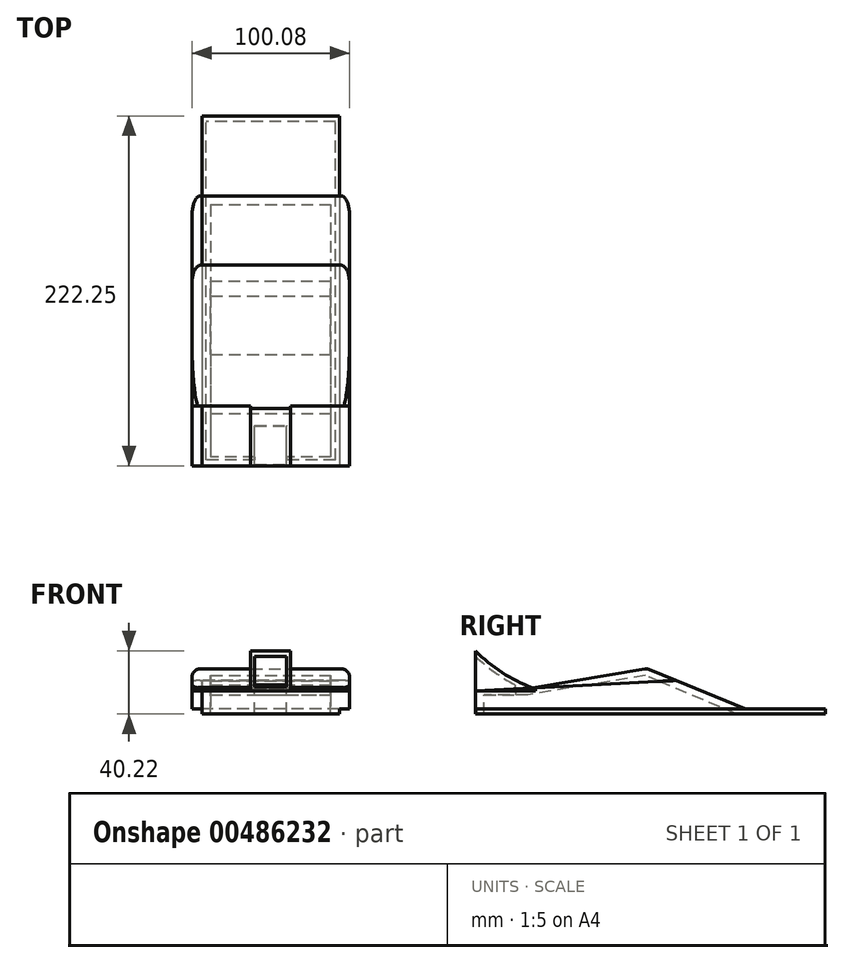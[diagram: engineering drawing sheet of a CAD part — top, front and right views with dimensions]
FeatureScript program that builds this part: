
annotation { "Feature Type Name" : "Feature", "Feature Type Description" : "" }
export const myFeature = defineFeature(function(context is Context, id is Id, definition is map)
    precondition{}
    {
        {
            var Q0;
            Q0=qCreatedBy(makeId("Top.planeOp"),FACE);
            var sketch = newSketch(context, id + "F0", { "sketchPlane" : qUnion([Q0])});
            skLineSegment(sketch, "E0.bottom", {"start": v(43.69, 111.12) * mm, "end": v(-43.69, 111.12) * mm});
            skLineSegment(sketch, "E0.top", {"start": v(43.69, -111.13) * mm, "end": v(-43.69, -111.13) * mm});
            skLineSegment(sketch, "E0.left", {"start": v(43.69, 111.12) * mm, "end": v(43.69, -111.13) * mm});
            skLineSegment(sketch, "E0.right", {"start": v(-43.69, 111.12) * mm, "end": v(-43.69, -111.13) * mm});
            skPoint(sketch, "E0.middle", {"position": v(0, 0) * mm});
            skSolve(sketch);
        }
        {
            var Q0;
            Q0 = qSketchRegion(id + "F0", true);
            extrude(context, id + "F1", {"entities" : qUnion([Q0]), "depth" : 3.17 * mm, "offsetDistance" : 25.4 * mm});
        }
        {
            var Q0;
            Q0=makeQuery(id+"F1.opExtrude","SWEPT_FACE",FACE,{"disambiguationData":[OSD([sQuery(id+"F0.wireOp",EDGE,"E0.right")])]});
            var sketch = newSketch(context, id + "F2", { "sketchPlane" : qUnion([Q0])});
            skLineSegment(sketch, "E1", {"start": v(-111.12, 3.18) * mm, "end": v(-60.32, 3.18) * mm, "construction": true});
            skLineSegment(sketch, "E2", {"start": v(-60.32, 3.18) * mm, "end": v(-16.2, 21.3) * mm});
            skLineSegment(sketch, "E3", {"start": v(-16.2, 21.3) * mm, "end": v(111.12, 14.82) * mm});
            skLineSegment(sketch, "E4", {"start": v(111.13, 3.18) * mm, "end": v(111.13, 14.82) * mm});
            skSolve(sketch);
        }
        {
            var Q0;
            {var subQ0=sQuery(id+"F2.wireOp",EDGE,"E2");Q0=makeQuery(id+"F2.imprint","IMPRINT",FACE,{"disambiguationData":[TD([[makeQuery(id+"F2.imprint","IMPRINT",EDGE,{"derivedFrom":subQ0}),-1.0]])]});}
            extrude(context, id + "F3", {"entities" : qUnion([Q0]), "depth" : 6.35 * mm, "offsetDistance" : 25.4 * mm});
        }
        {
            var Q0;
            Q0=makeQuery(id+"F3.opExtrude","CAP_FACE",FACE,{"disambiguationData":[OSD([sQuery(id+"F0.wireOp",EDGE,"E0.right"),sQuery(id+"F2.wireOp",EDGE,"E2"),sQuery(id+"F2.wireOp",EDGE,"E3"),sQuery(id+"F2.wireOp",EDGE,"E4")])],"isStart":true});
            extrude(context, id + "F4", {"entities" : qUnion([Q0]), "depth" : 87.38 * mm, "offsetDistance" : 25.4 * mm});
        }
        {
            var Q0;
            Q0=makeQuery(id+"F4.opExtrude","CAP_FACE",FACE,{"disambiguationData":[OSD([sQuery(id+"F0.wireOp",EDGE,"E0.right"),sQuery(id+"F2.wireOp",EDGE,"E2"),sQuery(id+"F2.wireOp",EDGE,"E3"),sQuery(id+"F2.wireOp",EDGE,"E4")])],"isStart":false});
            extrude(context, id + "F5", {"entities" : qUnion([Q0]), "operationType" : NewBodyOperationType.ADD, "depth" : 6.35 * mm, "offsetDistance" : 25.4 * mm});
        }
        {
            var Q0;
            Q0=makeQuery(id+"F5.opExtrude","CAP_FACE",FACE,{"disambiguationData":[OSD([sQuery(id+"F0.wireOp",EDGE,"E0.right"),sQuery(id+"F2.wireOp",EDGE,"E2"),sQuery(id+"F2.wireOp",EDGE,"E3"),sQuery(id+"F2.wireOp",EDGE,"E4")])],"isStart":false});
            var sketch = newSketch(context, id + "F6", { "sketchPlane" : qUnion([Q0])});
            skLineSegment(sketch, "E5", {"start": v(-111.13, 14.82) * mm, "end": v(-111.13, 40.22) * mm});
            skArc(sketch, "E6", {"start": v(-111.13, 40.22) * mm, "mid": v(-94.32, 26.4) * mm, "end": v(-74.87, 16.67) * mm});
            skLineSegment(sketch, "E7", {"start": v(16.2, 21.3) * mm, "end": v(-2.18, 28.86) * mm});
            skLineSegment(sketch, "E8", {"start": v(-2.18, 28.86) * mm, "end": v(-74.87, 16.67) * mm});
            skSolve(sketch);
        }
        {
            var Q0;
            {var subQ0=sQuery(id+"F6.wireOp",EDGE,"E5");Q0=makeQuery(id+"F6.imprint","IMPRINT",FACE,{"disambiguationData":[TD([[makeQuery(id+"F6.imprint","IMPRINT",EDGE,{"derivedFrom":subQ0}),-1.0]])]});}
            var Q1;
            {var subQ0=sQuery(id+"F6.wireOp",EDGE,"E7");Q1=makeQuery(id+"F6.imprint","IMPRINT",FACE,{"disambiguationData":[TD([[makeQuery(id+"F6.imprint","IMPRINT",EDGE,{"derivedFrom":subQ0}),1.0]])]});}
            extrude(context, id + "F7", {"entities" : qUnion([Q0, Q1]), "oppositeDirection" : true, "depth" : 100.08 * mm, "offsetDistance" : 25.4 * mm});
        }
        {
            var Q0;
            Q0=makeQuery(id+"F7.opExtrude","SWEPT_FACE",FACE,{"disambiguationData":[OSD([sQuery(id+"F6.wireOp",EDGE,"E5")])]});
            var sketch = newSketch(context, id + "F8", { "sketchPlane" : qUnion([Q0])});
            skLineSegment(sketch, "E9", {"start": v(-50.04, 40.22) * mm, "end": v(-50.04, 14.82) * mm});
            skLineSegment(sketch, "E10", {"start": v(-50.04, 45.23) * mm, "end": v(-81.4, 16.65) * mm});
            skLineSegment(sketch, "E11", {"start": v(-81.4, 16.65) * mm, "end": v(-50.04, 14.82) * mm});
            skLineSegment(sketch, "E12.MirrorCS", {"start": v(46.51, 14.82) * mm, "end": v(-4.16, 14.82) * mm});
            skLineSegment(sketch, "E13", {"start": v(0, 14.82) * mm, "end": v(12.7, 14.82) * mm});
            skLineSegment(sketch, "E14", {"start": v(0, 14.82) * mm, "end": v(-12.7, 14.82) * mm});
            skLineSegment(sketch, "E15", {"start": v(-12.7, 14.82) * mm, "end": v(-12.7, 47.79) * mm});
            skLineSegment(sketch, "E16", {"start": v(-12.7, 47.79) * mm, "end": v(-50.04, 45.23) * mm});
            skLineSegment(sketch, "E17", {"start": v(-12.7, 47.79) * mm, "end": v(0, 47.79) * mm});
            skLineSegment(sketch, "E18", {"start": v(0, 47.79) * mm, "end": v(0, 14.82) * mm});
            skLineSegment(sketch, "E19", {"start": v(12.7, 14.82) * mm, "end": v(12.7, 47.79) * mm});
            skLineSegment(sketch, "E20", {"start": v(12.7, 47.79) * mm, "end": v(0, 47.79) * mm});
            skLineSegment(sketch, "E21", {"start": v(12.7, 47.79) * mm, "end": v(40.72, 45.23) * mm});
            skLineSegment(sketch, "E22", {"start": v(46.51, 14.82) * mm, "end": v(-50.04, 14.82) * mm});
            skLineSegment(sketch, "E23", {"start": v(40.72, 45.23) * mm, "end": v(65.13, 48.77) * mm});
            skLineSegment(sketch, "E24", {"start": v(65.13, 48.77) * mm, "end": v(72.08, 16.65) * mm});
            skLineSegment(sketch, "E25", {"start": v(46.51, 14.82) * mm, "end": v(75.86, 14.82) * mm});
            skLineSegment(sketch, "E26", {"start": v(75.86, 14.82) * mm, "end": v(72.08, 16.65) * mm});
            skSolve(sketch);
        }
        {
            var Q0;
            {var subQ4=sQuery(id+"F8.wireOp",EDGE,"E9");Q0=makeQuery(id+"F8.imprint","IMPRINT",FACE,{"disambiguationData":[TD([[makeQuery(id+"F8.imprint","IMPRINT",EDGE,{"derivedFrom":subQ4}),1.0]])]});}
            var Q1;
            {var subQ0=sQuery(id+"F8.wireOp",EDGE,"E9");Q1=makeQuery(id+"F8.imprint","IMPRINT",FACE,{"disambiguationData":[TD([[makeQuery(id+"F8.imprint","IMPRINT",EDGE,{"derivedFrom":subQ0}),-1.0]])]});}
            var Q2;
            {var subQ0=sQuery(id+"F8.wireOp",EDGE,"E12.MirrorCS");var subQ1=sQuery(id+"F8.wireOp",EDGE,"6b0f6dcd-051e-4a31-8ef7-d305b529bc940.MirrorCS");var subQ2=makeQuery(id+"F8.imprint","INTERSECT",VERTEX,{"derivedFrom":[subQ1,subQ0]});Q2=makeQuery(id+"F8.imprint","IMPRINT",FACE,{"disambiguationData":[TD([[makeQuery(id+"F8.imprint","IMPRINT",EDGE,{"disambiguationData":[TD([[subQ2,1.0]])],"derivedFrom":subQ1}),-1.0]])]});}
            var Q3;
            {var subQ0=sQuery(id+"F8.wireOp",EDGE,"E21");Q3=makeQuery(id+"F8.imprint","IMPRINT",FACE,{"disambiguationData":[TD([[makeQuery(id+"F8.imprint","IMPRINT",EDGE,{"derivedFrom":subQ0}),-1.0]])]});}
            var Q4;
            {var subQ1=sQuery(id+"F6.wireOp",EDGE,"E5");var subQ2=makeQuery(id+"F7.opExtrude","CAP_EDGE",EDGE,{"disambiguationData":[OSD([subQ1])],"isStart":true});Q4=makeQuery(id+"F8.imprint","IMPRINT",FACE,{"disambiguationData":[TD([[makeQuery(id+"F8.imprint","IMPRINT",EDGE,{"derivedFrom":subQ2}),1.0]])]});}
            extrude(context, id + "F9", {"entities" : qUnion([Q0, Q1, Q2, Q3, Q4]), "operationType" : NewBodyOperationType.REMOVE, "oppositeDirection" : true, "depth" : 38.1 * mm, "offsetDistance" : 25.4 * mm});
        }
        {
            var Q0;
            Q0=makeQuery(id+"F1.opExtrude","CAP_FACE",FACE,{"disambiguationData":[OSD([sQuery(id+"F0.wireOp",EDGE,"E0.bottom"),sQuery(id+"F0.wireOp",EDGE,"E0.top"),sQuery(id+"F0.wireOp",EDGE,"E0.left"),sQuery(id+"F0.wireOp",EDGE,"E0.right")])],"isStart":true});
            var sketch = newSketch(context, id + "F10", { "sketchPlane" : qUnion([Q0])});
            skLineSegment(sketch, "E27.bottom", {"start": v(41.08, 107.56) * mm, "end": v(-41.08, 107.56) * mm});
            skLineSegment(sketch, "E27.top", {"start": v(41.08, -107.56) * mm, "end": v(-41.08, -107.56) * mm});
            skLineSegment(sketch, "E27.left", {"start": v(41.08, 107.56) * mm, "end": v(41.08, -107.56) * mm});
            skLineSegment(sketch, "E27.right", {"start": v(-41.08, 107.56) * mm, "end": v(-41.08, -107.56) * mm});
            skPoint(sketch, "E27.middle", {"position": v(0, 0) * mm});
            skSolve(sketch);
        }
        {
            var Q0;
            Q0 = qSketchRegion(id + "F10", true);
            extrude(context, id + "F11", {"entities" : qUnion([Q0]), "operationType" : NewBodyOperationType.REMOVE, "oppositeDirection" : true, "depth" : 0.03 * mm, "offsetDistance" : 25.4 * mm});
        }
        {
            var Q0;
            Q0=qCreatedBy(makeId("Right.planeOp"),FACE);
            var sketch = newSketch(context, id + "F12", { "sketchPlane" : qUnion([Q0])});
            skLineSegment(sketch, "E28", {"start": v(54.76, 0) * mm, "end": v(-3.2, 24.58) * mm});
            skLineSegment(sketch, "E29", {"start": v(-3.2, 24.58) * mm, "end": v(-77.88, 12.23) * mm});
            skLineSegment(sketch, "E30", {"start": v(-105.64, 27.93) * mm, "end": v(-105.64, 0) * mm});
            skLineSegment(sketch, "E31", {"start": v(-105.64, 0) * mm, "end": v(54.76, 0) * mm});
            skLineSegment(sketch, "E32", {"start": v(-77.88, 12.23) * mm, "end": v(-105.64, 12.23) * mm});
            skSolve(sketch);
        }
        {
            var Q0;
            Q0 = qSketchRegion(id + "F12", true);
            extrude(context, id + "F13", {"entities" : qUnion([Q0]), "operationType" : NewBodyOperationType.REMOVE, "oppositeDirection" : true, "depth" : 76.2 * mm, "offsetDistance" : 25.4 * mm, "symmetric" : true});
        }
        {
            var Q0;
            Q0=makeQuery(id+"F7.opExtrude","SWEPT_FACE",FACE,{"disambiguationData":[OSD([sQuery(id+"F6.wireOp",EDGE,"E5")])]});
            shell(context, id + "F14", {"entities" : qUnion([Q0]), "thickness" : 2.54 * mm});
        }
        {
            var Q0;
            Q0=makeQuery(id+"F14.opShell","OFFSET_FACE",FACE,{"disambiguationData":[OSD([sQuery(id+"F2.wireOp",EDGE,"E3")])]});
            extrude(context, id + "F15", {"entities" : qUnion([Q0]), "operationType" : NewBodyOperationType.REMOVE, "oppositeDirection" : true, "depth" : 25.4 * mm, "offsetDistance" : 25.4 * mm});
        }
        {
            var Q0;
            Q0=makeQuery(id+"F7.opExtrude","CAP_EDGE",EDGE,{"disambiguationData":[OSD([sQuery(id+"F6.wireOp",EDGE,"E7")])],"isStart":false});
            var Q1;
            Q1=makeQuery(id+"F3.opExtrude","CAP_EDGE",EDGE,{"disambiguationData":[OSD([sQuery(id+"F2.wireOp",EDGE,"E2")])],"isStart":false});
            var Q2;
            Q2=makeQuery(id+"F7.opExtrude","CAP_EDGE",EDGE,{"disambiguationData":[OSD([sQuery(id+"F6.wireOp",EDGE,"E8")])],"isStart":false});
            var Q3;
            Q3=makeQuery(id+"F5.opExtrude","CAP_EDGE",EDGE,{"disambiguationData":[OSD([sQuery(id+"F2.wireOp",EDGE,"E2")])],"isStart":false});
            var Q4;
            Q4=makeQuery(id+"F7.opExtrude","CAP_EDGE",EDGE,{"disambiguationData":[OSD([sQuery(id+"F6.wireOp",EDGE,"E7")])],"isStart":true});
            var Q5;
            Q5=makeQuery(id+"F7.opExtrude","CAP_EDGE",EDGE,{"disambiguationData":[OSD([sQuery(id+"F6.wireOp",EDGE,"E8")])],"isStart":true});
            var Q6;
            Q6=makeQuery(id+"F7.opExtrude","SWEPT_EDGE",EDGE,{"disambiguationData":[OSD([sQuery(id+"F6.wireOp",EDGE,"E7"),sQuery(id+"F6.wireOp",EDGE,"E8")])]});
            fillet(context, id + "F16", {"entities" : qUnion([Q0, Q1, Q2, Q3, Q4, Q5, Q6]), "tangentPropagation" : true, "radius" : 5.08 * mm, "defaultsChanged" : false, "vertexSettings" : [], "allowEdgeOverflow" : false});
        }
    });
